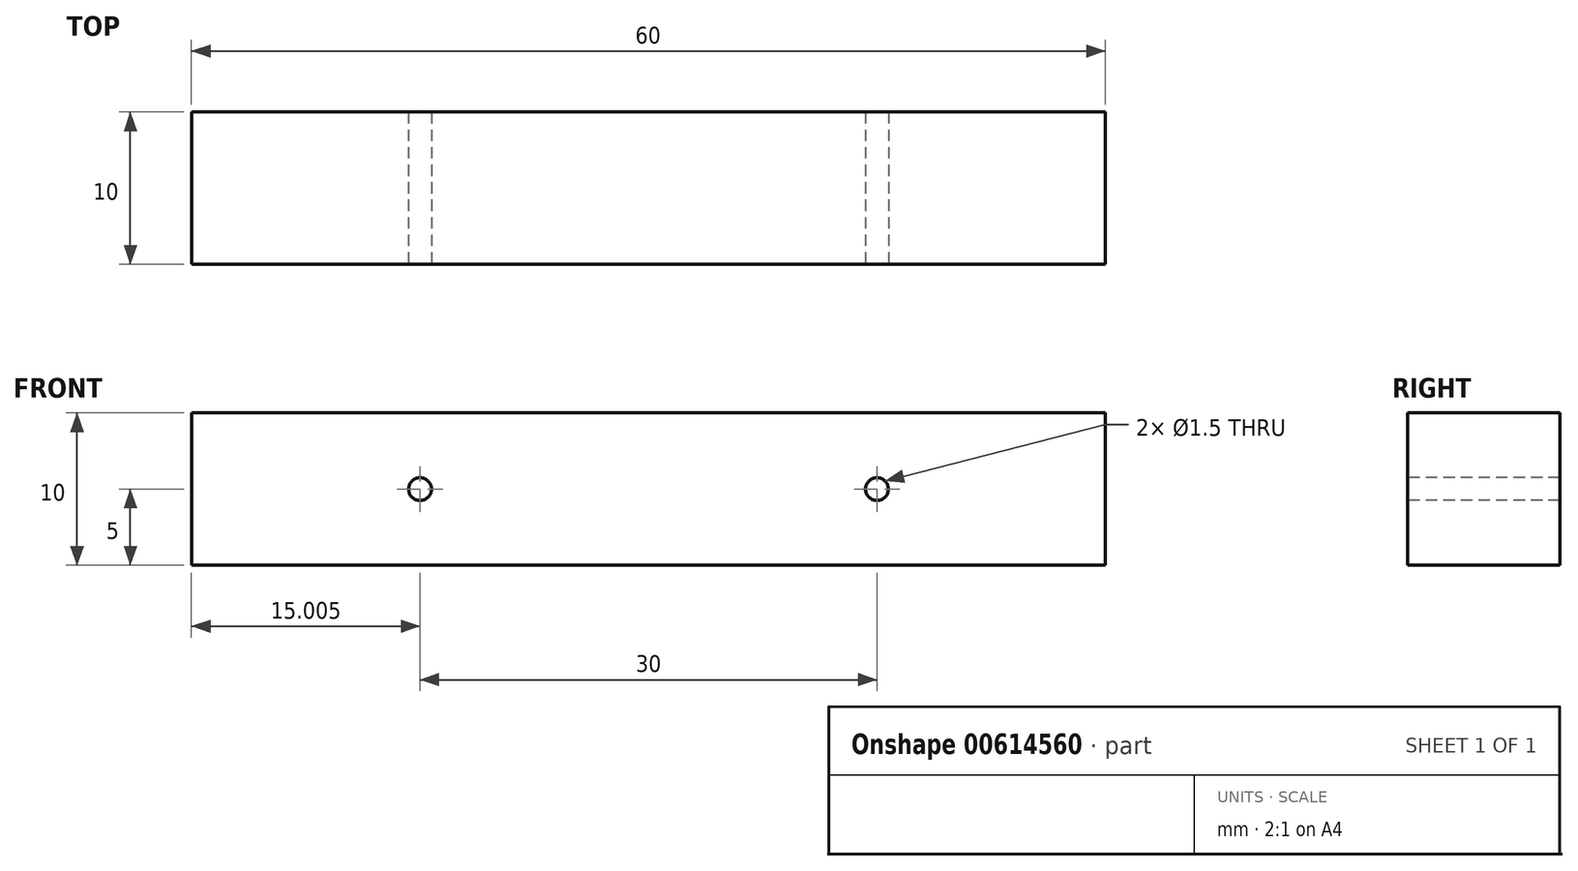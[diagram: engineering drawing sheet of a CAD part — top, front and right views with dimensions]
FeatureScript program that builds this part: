
annotation { "Feature Type Name" : "Feature", "Feature Type Description" : "" }
export const myFeature = defineFeature(function(context is Context, id is Id, definition is map)
    precondition{}
    {
        {
            var Q0;
            Q0=qCreatedBy(makeId("Front.planeOp"),FACE);
            var sketch = newSketch(context, id + "F0", { "sketchPlane" : qUnion([Q0])});
            skLineSegment(sketch, "E0.bottom", {"start": v(-60.5, 8.12) * mm, "end": v(-0.5, 8.12) * mm});
            skLineSegment(sketch, "E0.top", {"start": v(-60.5, -1.88) * mm, "end": v(-0.5, -1.88) * mm});
            skLineSegment(sketch, "E0.left", {"start": v(-60.5, 8.12) * mm, "end": v(-60.5, -1.88) * mm});
            skLineSegment(sketch, "E0.right", {"start": v(-0.5, 8.12) * mm, "end": v(-0.5, -1.88) * mm});
            skLineSegment(sketch, "E1", {"start": v(-45.5, -1.88) * mm, "end": v(-45.5, 8.12) * mm});
            skLineSegment(sketch, "E2", {"start": v(-15.5, -1.88) * mm, "end": v(-15.5, 8.12) * mm});
            skSolve(sketch);
        }
        {
            var Q0;
            Q0 = qSketchRegion(id + "F0", true);
            extrude(context, id + "F1", {"entities" : qUnion([Q0]), "depth" : 10 * mm, "offsetDistance" : 25 * mm});
        }
        {
            var Q0;
            Q0=makeQuery(id+"F1.opExtrude","CAP_FACE",FACE,{"disambiguationData":[OSD([sQuery(id+"F0.wireOp",EDGE,"E0.bottom"),sQuery(id+"F0.wireOp",EDGE,"E0.top"),sQuery(id+"F0.wireOp",EDGE,"E0.left"),sQuery(id+"F0.wireOp",EDGE,"E0.right")])],"isStart":false});
            var sketch = newSketch(context, id + "F2", { "sketchPlane" : qUnion([Q0])});
            skCircle(sketch, "E3", {"center": v(-45.5, 3.12) * mm, "radius": 0.75 * mm});
            skCircle(sketch, "E4", {"center": v(-15.5, 3.12) * mm, "radius": 0.75 * mm});
            skSolve(sketch);
        }
        {
            var Q0;
            Q0=sQuery(id+"F2.wireOp",VERTEX,"E3.center");
            var Q1;
            Q1=makeQuery(id+"F1.opExtrude","SWEPT_BODY",BODY,{"disambiguationData":[OSD([sQuery(id+"F0.wireOp",EDGE,"E0.bottom"),sQuery(id+"F0.wireOp",EDGE,"E0.top"),sQuery(id+"F0.wireOp",EDGE,"E0.left"),sQuery(id+"F0.wireOp",EDGE,"E0.right")])]});
            hole(context, id + "F3", {"style" : HoleStyle.SIMPLE, "endStyle" : HoleEndStyle.BLIND, "holeDiameter" : 1.5 * mm, "majorDiameter" : 5 * mm, "holeDepth" : 5 * mm, "isTappedThrough" : true, "tappedDepth" : 12 * mm, "tapClearance" : 3, "locations" : qUnion([Q0]), "scope" : qUnion([Q1])});
        }
        {
            var Q0;
            Q0 = qSketchRegion(id + "F2", true);
            extrude(context, id + "F4", {"entities" : qUnion([Q0]), "operationType" : NewBodyOperationType.REMOVE, "oppositeDirection" : true, "depth" : 25 * mm, "offsetDistance" : 25 * mm});
        }
    });
